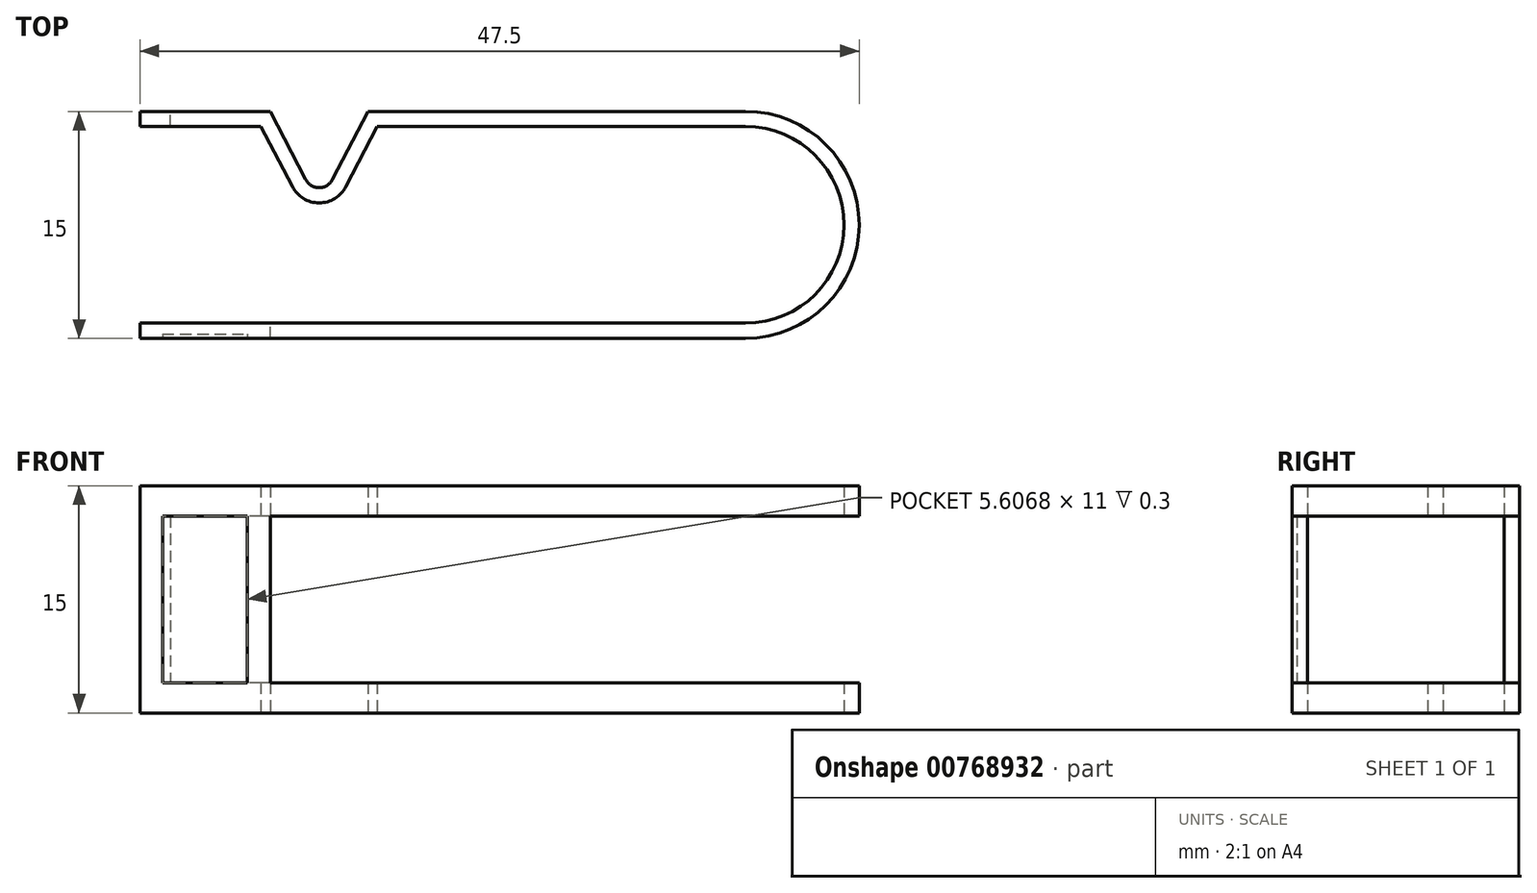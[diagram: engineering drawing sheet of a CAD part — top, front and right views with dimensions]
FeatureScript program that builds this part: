
annotation { "Feature Type Name" : "Feature", "Feature Type Description" : "" }
export const myFeature = defineFeature(function(context is Context, id is Id, definition is map)
    precondition{}
    {
        {
            var Q0;
            Q0=qCreatedBy(makeId("Top.planeOp"),FACE);
            var sketch = newSketch(context, id + "F0", { "sketchPlane" : qUnion([Q0])});
            skLineSegment(sketch, "E0.bottom", {"start": v(0, 0) * mm, "end": v(40, 0) * mm});
            skLineSegment(sketch, "E0.top", {"start": v(0, 15) * mm, "end": v(8.6, 15) * mm});
            skArc(sketch, "E1", {"start": v(40, 0) * mm, "mid": v(47.5, 7.5) * mm, "end": v(40, 15) * mm});
            skLineSegment(sketch, "E2", {"start": v(8.6, 15) * mm, "end": v(10.95, 10.5) * mm});
            skLineSegment(sketch, "E3", {"start": v(12.73, 10.5) * mm, "end": v(15.07, 15) * mm});
            skLineSegment(sketch, "E4.trimOffspring", {"start": v(15.07, 15) * mm, "end": v(40, 15) * mm});
            skPoint(sketch, "E5.visualSharp", {"position": v(11.84, 8.8) * mm});
            skArc(sketch, "E5.filletArc", {"start": v(10.95, 10.5) * mm, "mid": v(11.84, 9.96) * mm, "end": v(12.73, 10.5) * mm});
            skLineSegment(sketch, "E6.0", {"start": v(13.61, 10.03) * mm, "end": v(15.68, 14) * mm});
            skArc(sketch, "E6.1", {"start": v(10.07, 10.03) * mm, "mid": v(11.84, 8.96) * mm, "end": v(13.61, 10.03) * mm});
            skLineSegment(sketch, "E6.2", {"start": v(15.68, 14) * mm, "end": v(40, 14) * mm});
            skLineSegment(sketch, "E6.3", {"start": v(8, 14) * mm, "end": v(10.07, 10.03) * mm});
            skArc(sketch, "E6.4", {"start": v(40, 1) * mm, "mid": v(46.5, 7.5) * mm, "end": v(40, 14) * mm});
            skLineSegment(sketch, "E6.5", {"start": v(0, 1) * mm, "end": v(40, 1) * mm});
            skLineSegment(sketch, "E6.7", {"start": v(0, 14) * mm, "end": v(8, 14) * mm});
            skLineSegment(sketch, "E7", {"start": v(0, 15) * mm, "end": v(0, 14) * mm});
            skLineSegment(sketch, "E8", {"start": v(0, 1) * mm, "end": v(0, 0) * mm});
            skSolve(sketch);
        }
        {
            var Q0;
            Q0=makeQuery(id+"F0.imprint","IMPRINT",FACE,{"disambiguationData":[TD([[makeQuery(id+"F0.imprint","IMPRINT",EDGE,{"derivedFrom":sQuery(id+"F0.wireOp",EDGE,"E0.bottom")}),1.0]])]});
            extrude(context, id + "F1", {"entities" : qUnion([Q0]), "depth" : 15 * mm, "offsetDistance" : 25 * mm});
        }
        {
            var Q0;
            Q0=makeQuery(id+"F1.opExtrude","SWEPT_FACE",FACE,{"disambiguationData":[OSD([sQuery(id+"F0.wireOp",EDGE,"E4.trimOffspring")])]});
            var sketch = newSketch(context, id + "F2", { "sketchPlane" : qUnion([Q0])});
            skLineSegment(sketch, "E9.bottom", {"start": v(-47.5, 13) * mm, "end": v(-8.6, 13) * mm});
            skLineSegment(sketch, "E9.top", {"start": v(-47.5, 2) * mm, "end": v(-8.6, 2) * mm});
            skLineSegment(sketch, "E9.left", {"start": v(-47.5, 13) * mm, "end": v(-47.5, 2) * mm});
            skLineSegment(sketch, "E9.right", {"start": v(-8.6, 13) * mm, "end": v(-8.6, 2) * mm});
            skSolve(sketch);
        }
        {
            var Q0;
            {var subQ0=sQuery(id+"F2.wireOp",EDGE,"E9.left");Q0=makeQuery(id+"F2.imprint","IMPRINT",FACE,{"disambiguationData":[TD([[makeQuery(id+"F2.imprint","IMPRINT",EDGE,{"derivedFrom":subQ0}),1.0]])]});}
            var Q1;
            {var subQ0=sQuery(id+"F2.wireOp",EDGE,"E9.bottom");var subQ1=sQuery(id+"F0.wireOp",EDGE,"E4.trimOffspring");var subQ2=makeQuery(id+"F1.opExtrude","SWEPT_EDGE",EDGE,{"disambiguationData":[OSD([sQuery(id+"F0.wireOp",EDGE,"E1"),subQ1])]});var subQ3=makeQuery(id+"F2.imprint","INTERSECT",VERTEX,{"derivedFrom":[subQ2,subQ0]});Q1=makeQuery(id+"F2.imprint","IMPRINT",FACE,{"disambiguationData":[TD([[makeQuery(id+"F2.imprint","IMPRINT",EDGE,{"disambiguationData":[TD([[subQ3,-1.0]])],"derivedFrom":subQ0}),-1.0]])]});}
            var Q2;
            {var subQ0=sQuery(id+"F2.wireOp",EDGE,"E9.right");Q2=makeQuery(id+"F2.imprint","IMPRINT",FACE,{"disambiguationData":[TD([[makeQuery(id+"F2.imprint","IMPRINT",EDGE,{"derivedFrom":subQ0}),-1.0]])]});}
            extrude(context, id + "F3", {"entities" : qUnion([Q0, Q1, Q2]), "operationType" : NewBodyOperationType.REMOVE, "oppositeDirection" : true, "depth" : 25 * mm, "offsetDistance" : 25 * mm});
        }
        {
            var Q0;
            Q0=makeQuery(id+"F1.opExtrude","SWEPT_FACE",FACE,{"disambiguationData":[OSD([sQuery(id+"F0.wireOp",EDGE,"E0.top")])]});
            var sketch = newSketch(context, id + "F4", { "sketchPlane" : qUnion([Q0])});
            skLineSegment(sketch, "E10.bottom", {"start": v(-8.6, 13) * mm, "end": v(-2, 13) * mm});
            skLineSegment(sketch, "E10.top", {"start": v(-8.6, 2) * mm, "end": v(-2, 2) * mm});
            skLineSegment(sketch, "E10.left", {"start": v(-8.6, 13) * mm, "end": v(-8.6, 2) * mm});
            skLineSegment(sketch, "E10.right", {"start": v(-2, 13) * mm, "end": v(-2, 2) * mm});
            skSolve(sketch);
        }
        {
            var Q0;
            Q0=makeQuery(id+"F4.imprint","IMPRINT",FACE,{"disambiguationData":[TD([[makeQuery(id+"F4.imprint","IMPRINT",EDGE,{"derivedFrom":sQuery(id+"F4.wireOp",EDGE,"E10.bottom")}),-1.0]])]});
            extrude(context, id + "F5", {"entities" : qUnion([Q0]), "operationType" : NewBodyOperationType.REMOVE, "oppositeDirection" : true, "depth" : 3 * mm, "offsetDistance" : 25 * mm});
        }
        {
            var Q0;
            Q0=makeQuery(id+"F1.opExtrude","SWEPT_FACE",FACE,{"disambiguationData":[OSD([sQuery(id+"F0.wireOp",EDGE,"E0.bottom")])]});
            var sketch = newSketch(context, id + "F6", { "sketchPlane" : qUnion([Q0])});
            skLineSegment(sketch, "E11.bottom", {"start": v(1.5, 13) * mm, "end": v(7.1, 13) * mm});
            skLineSegment(sketch, "E11.top", {"start": v(1.5, 2) * mm, "end": v(7.1, 2) * mm});
            skLineSegment(sketch, "E11.left", {"start": v(1.5, 13) * mm, "end": v(1.5, 2) * mm});
            skLineSegment(sketch, "E11.right", {"start": v(7.1, 13) * mm, "end": v(7.1, 2) * mm});
            skSolve(sketch);
        }
        {
            var Q0;
            Q0=makeQuery(id+"F6.imprint","IMPRINT",FACE,{"disambiguationData":[TD([[makeQuery(id+"F6.imprint","IMPRINT",EDGE,{"derivedFrom":sQuery(id+"F6.wireOp",EDGE,"E11.bottom")}),-1.0]])]});
            extrude(context, id + "F7", {"entities" : qUnion([Q0]), "operationType" : NewBodyOperationType.REMOVE, "oppositeDirection" : true, "depth" : 0.3 * mm, "offsetDistance" : 25 * mm});
        }
    });
